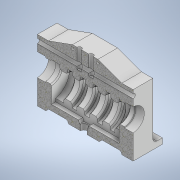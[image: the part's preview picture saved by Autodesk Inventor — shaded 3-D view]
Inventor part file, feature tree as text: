
AUTODESK INVENTOR PART (.ipt)
format: ipt  version: 2022 (Build 260153000, 153)  size: 425,984 bytes
history: native  units: mm
features: sketch x10, extrude x4, hole x4, fillet x2, revolve x2, other x1, chamfer x1
ambient origin geometry x8: Origin, YZ Plane, XZ Plane, XY Plane, X Axis, Y Axis, Z Axis, Center Point
bodies: Body1 (feature_tree)
feature tree (24):
  other  "Твердое тело1"
  extrude  "Выдавливание1"  Depth=170.0mm
  extrude  "Выдавливание2"  Depth=110.0mm
  fillet  "Сопряжение1"  Radius=45.0mm
  extrude  "Выдавливание3"  Depth=27.925268mm
  fillet  "Сопряжение2"  Radius=27.925268mm
  chamfer  "Фаска1"  Distance=20.0mm
  hole  "Отверстие1"  [1 undecoded]
  hole  "Отверстие2"  [1 undecoded]
  hole  "Отверстие3"  [1 undecoded]
  revolve  "Вращение2"
  extrude  "Выдавливание4"  Depth=170.0mm TaperAngle=0.0deg
  hole  "Отверстие4"  [1 undecoded]
  revolve  "Вращение4"
  sketch  "Эскиз1"
  sketch  "Эскиз2"
  sketch  "Эскиз3"
  sketch  "Эскиз4"
  sketch  "Эскиз5"
  sketch  "Эскиз6"
  sketch  "Эскиз7"
  sketch  "Эскиз9"
  sketch  "Эскиз10"
  sketch  "Эскиз11"
note: 4 required parameter values undecoded (feature->parameter linkage not recoverable at this tier; creation-order binding heuristic only, values carry confidence <= 0.55)
